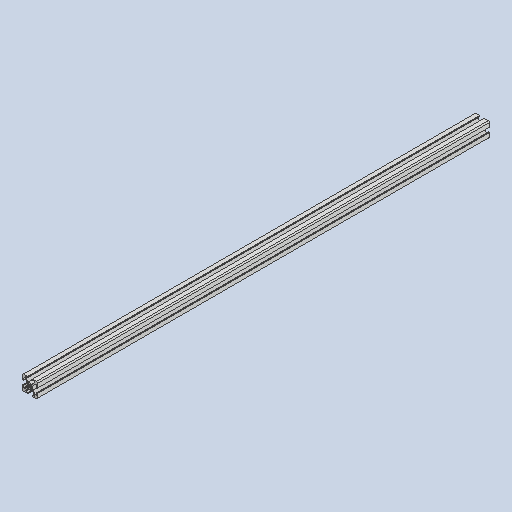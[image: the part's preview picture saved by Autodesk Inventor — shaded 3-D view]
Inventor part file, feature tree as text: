
AUTODESK INVENTOR PART (.ipt)
format: ipt  version: 2022 (Build 260153000, 153)  size: 279,552 bytes
history: native  units: in
note: dims shown in document units (in); Inventor stores cm internally (conversion verified against a paired STEP export)
features: other x3, plane x2, sketch x1
ambient origin geometry x8: Origin, YZ Plane, XZ Plane, XY Plane, X Axis, Y Axis, Z Axis, Center Point
bodies: Solid1 (feature_tree)
feature tree (6):
  other  "20x20x600 T Slot Extrusion Bar.ipt"
  other  "Solid1::20x20x600 T Slot Extrusion Bar.ipt"
  other  "TaggingFeature1"
  sketch  "Sketch_1"  dims[d0=0.3937in]
  plane  "Work Plane1"
  plane  "Work Plane2"
